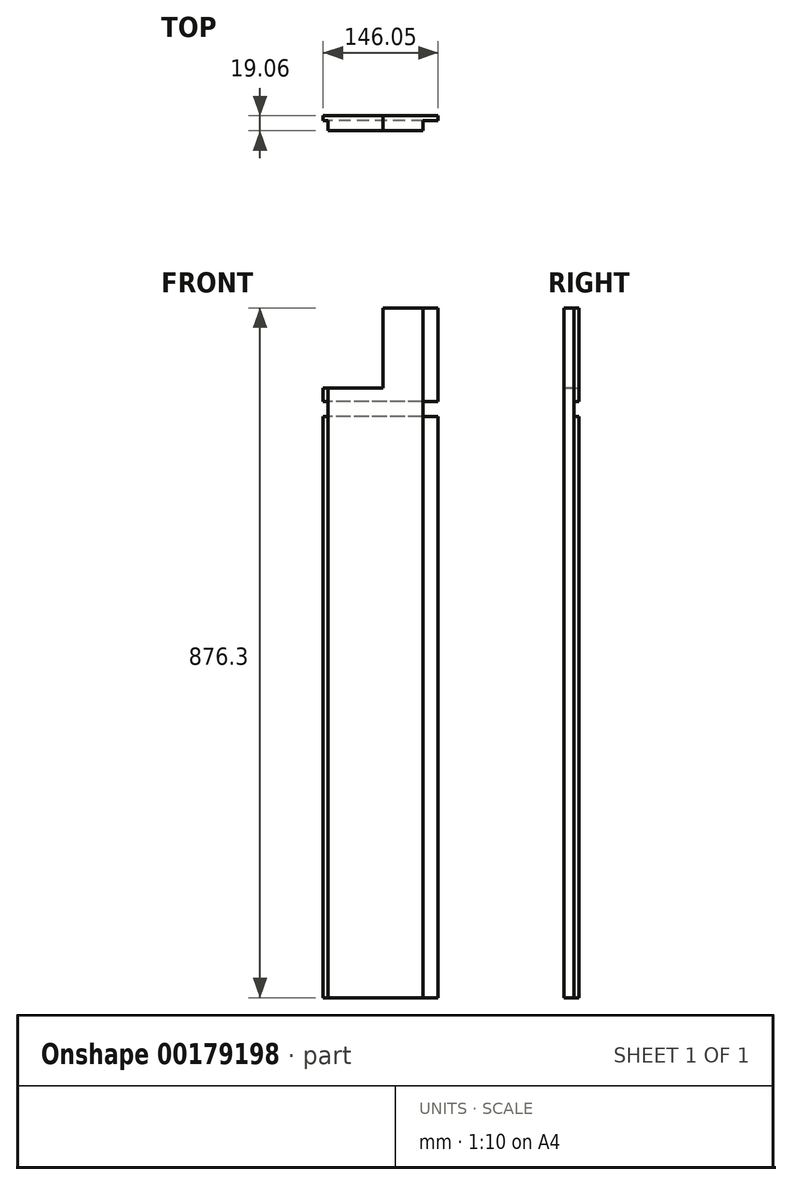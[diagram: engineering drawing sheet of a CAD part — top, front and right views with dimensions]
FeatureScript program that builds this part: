
annotation { "Feature Type Name" : "Feature", "Feature Type Description" : "" }
export const myFeature = defineFeature(function(context is Context, id is Id, definition is map)
    precondition{}
    {
        {
            var Q0;
            Q0=qCreatedBy(makeId("Front.planeOp"),FACE);
            var sketch = newSketch(context, id + "F0", { "sketchPlane" : qUnion([Q0])});
            skLineSegment(sketch, "E0.bottom", {"start": v(-247.9, 438.15) * mm, "end": v(-101.85, 438.15) * mm});
            skLineSegment(sketch, "E0.top", {"start": v(-247.9, -438.15) * mm, "end": v(-101.85, -438.15) * mm});
            skLineSegment(sketch, "E0.left", {"start": v(-247.9, 438.15) * mm, "end": v(-247.9, -438.15) * mm});
            skLineSegment(sketch, "E0.right", {"start": v(-101.85, 438.15) * mm, "end": v(-101.85, -438.15) * mm});
            skLineSegment(sketch, "E1", {"start": v(-247.9, 0) * mm, "end": v(-101.85, 0) * mm});
            skSolve(sketch);
        }
        {
            var Q0;
            {var subQ0=sQuery(id+"F0.wireOp",EDGE,"E0.bottom");Q0=makeQuery(id+"F0.imprint","IMPRINT",FACE,{"disambiguationData":[TD([[makeQuery(id+"F0.imprint","IMPRINT",EDGE,{"derivedFrom":subQ0}),-1.0]])]});}
            var Q1;
            {var subQ0=sQuery(id+"F0.wireOp",EDGE,"E0.top");Q1=makeQuery(id+"F0.imprint","IMPRINT",FACE,{"disambiguationData":[TD([[makeQuery(id+"F0.imprint","IMPRINT",EDGE,{"derivedFrom":subQ0}),1.0]])]});}
            extrude(context, id + "F1", {"entities" : qUnion([Q0, Q1]), "depth" : 19.05 * mm, "symmetric" : true});
        }
        {
            var Q0;
            Q0=makeQuery(id+"F1.opExtrude","CAP_FACE",FACE,{"disambiguationData":[OSD([sQuery(id+"F0.wireOp",EDGE,"E0.bottom"),sQuery(id+"F0.wireOp",EDGE,"E0.top"),sQuery(id+"F0.wireOp",EDGE,"E0.left"),sQuery(id+"F0.wireOp",EDGE,"E0.right")])],"isStart":true});
            var sketch = newSketch(context, id + "F2", { "sketchPlane" : qUnion([Q0])});
            skLineSegment(sketch, "E2.bottom", {"start": v(101.85, 300.04) * mm, "end": v(247.9, 300.04) * mm});
            skLineSegment(sketch, "E2.top", {"start": v(101.85, 319.09) * mm, "end": v(247.9, 319.09) * mm});
            skLineSegment(sketch, "E2.left", {"start": v(101.85, 300.04) * mm, "end": v(101.85, 319.09) * mm});
            skLineSegment(sketch, "E2.right", {"start": v(247.9, 300.04) * mm, "end": v(247.9, 319.09) * mm});
            skSolve(sketch);
        }
        {
            var Q0;
            Q0=makeQuery(id+"F2.imprint","IMPRINT",FACE,{"disambiguationData":[TD([[makeQuery(id+"F2.imprint","IMPRINT",EDGE,{"derivedFrom":sQuery(id+"F2.wireOp",EDGE,"E2.bottom")}),1.0]])]});
            extrude(context, id + "F3", {"entities" : qUnion([Q0]), "operationType" : NewBodyOperationType.REMOVE, "oppositeDirection" : true, "depth" : 6.35 * mm});
        }
        {
            var Q0;
            Q0=makeQuery(id+"F1.opExtrude","CAP_FACE",FACE,{"disambiguationData":[OSD([sQuery(id+"F0.wireOp",EDGE,"E0.bottom"),sQuery(id+"F0.wireOp",EDGE,"E0.top"),sQuery(id+"F0.wireOp",EDGE,"E0.left"),sQuery(id+"F0.wireOp",EDGE,"E0.right")])],"isStart":false});
            var sketch = newSketch(context, id + "F4", { "sketchPlane" : qUnion([Q0])});
            skLineSegment(sketch, "E3.bottom", {"start": v(-101.85, 438.15) * mm, "end": v(-120.9, 438.15) * mm});
            skLineSegment(sketch, "E3.top", {"start": v(-101.85, -438.15) * mm, "end": v(-120.9, -438.15) * mm});
            skLineSegment(sketch, "E3.left", {"start": v(-101.85, 438.15) * mm, "end": v(-101.85, -438.15) * mm});
            skLineSegment(sketch, "E3.right", {"start": v(-120.9, 438.15) * mm, "end": v(-120.9, -438.15) * mm});
            skSolve(sketch);
        }
        {
            var Q0;
            Q0=makeQuery(id+"F4.imprint","IMPRINT",FACE,{"disambiguationData":[TD([[makeQuery(id+"F4.imprint","IMPRINT",EDGE,{"derivedFrom":sQuery(id+"F4.wireOp",EDGE,"E3.bottom")}),-1.0]])]});
            extrude(context, id + "F5", {"entities" : qUnion([Q0]), "operationType" : NewBodyOperationType.REMOVE, "oppositeDirection" : true, "depth" : 12.7 * mm});
        }
        {
            var Q0;
            Q0=makeQuery(id+"F1.opExtrude","CAP_FACE",FACE,{"disambiguationData":[OSD([sQuery(id+"F0.wireOp",EDGE,"E0.bottom"),sQuery(id+"F0.wireOp",EDGE,"E0.top"),sQuery(id+"F0.wireOp",EDGE,"E0.left"),sQuery(id+"F0.wireOp",EDGE,"E0.right")])],"isStart":false});
            var sketch = newSketch(context, id + "F6", { "sketchPlane" : qUnion([Q0])});
            skLineSegment(sketch, "E4.bottom", {"start": v(-247.9, 438.15) * mm, "end": v(-241.55, 438.15) * mm});
            skLineSegment(sketch, "E4.top", {"start": v(-247.9, -438.15) * mm, "end": v(-241.55, -438.15) * mm});
            skLineSegment(sketch, "E4.left", {"start": v(-247.9, 438.15) * mm, "end": v(-247.9, -438.15) * mm});
            skLineSegment(sketch, "E4.right", {"start": v(-241.55, 438.15) * mm, "end": v(-241.55, -438.15) * mm});
            skSolve(sketch);
        }
        {
            var Q0;
            Q0=makeQuery(id+"F6.imprint","IMPRINT",FACE,{"disambiguationData":[TD([[makeQuery(id+"F6.imprint","IMPRINT",EDGE,{"derivedFrom":sQuery(id+"F6.wireOp",EDGE,"E4.bottom")}),-1.0]])]});
            extrude(context, id + "F7", {"entities" : qUnion([Q0]), "operationType" : NewBodyOperationType.REMOVE, "oppositeDirection" : true, "depth" : 12.7 * mm});
        }
        {
            var Q0;
            {var subQ0=sQuery(id+"F0.wireOp",EDGE,"E0.top");var subQ1=sQuery(id+"F0.wireOp",EDGE,"E0.left");var subQ2=sQuery(id+"F0.wireOp",EDGE,"E0.right");Q0=makeQuery(id+"F3.boolean.opBoolean","SPLIT",FACE,{"disambiguationData":[TD([makeQuery(id+"F1.opExtrude","SWEPT_FACE",FACE,{"disambiguationData":[OSD([subQ0])]})])],"derivedFrom":makeQuery(id+"F1.opExtrude","CAP_FACE",FACE,{"disambiguationData":[OSD([sQuery(id+"F0.wireOp",EDGE,"E0.bottom"),subQ0,subQ1,subQ2])],"isStart":true})});}
            var sketch = newSketch(context, id + "F8", { "sketchPlane" : qUnion([Q0])});
            skLineSegment(sketch, "E5.bottom", {"start": v(171.7, 438.15) * mm, "end": v(247.9, 438.15) * mm});
            skLineSegment(sketch, "E5.top", {"start": v(171.7, 336.55) * mm, "end": v(247.9, 336.55) * mm});
            skLineSegment(sketch, "E5.left", {"start": v(171.7, 438.15) * mm, "end": v(171.7, 336.55) * mm});
            skLineSegment(sketch, "E5.right", {"start": v(247.9, 438.15) * mm, "end": v(247.9, 336.55) * mm});
            skSolve(sketch);
        }
        {
            var Q0;
            Q0=makeQuery(id+"F8.imprint","IMPRINT",FACE,{"disambiguationData":[TD([[makeQuery(id+"F8.imprint","IMPRINT",EDGE,{"derivedFrom":sQuery(id+"F8.wireOp",EDGE,"E5.bottom")}),-1.0]])]});
            extrude(context, id + "F9", {"entities" : qUnion([Q0]), "operationType" : NewBodyOperationType.REMOVE, "endBound" : BoundingType.THROUGH_ALL, "oppositeDirection" : true, "depth" : 25.4 * mm});
        }
    });
